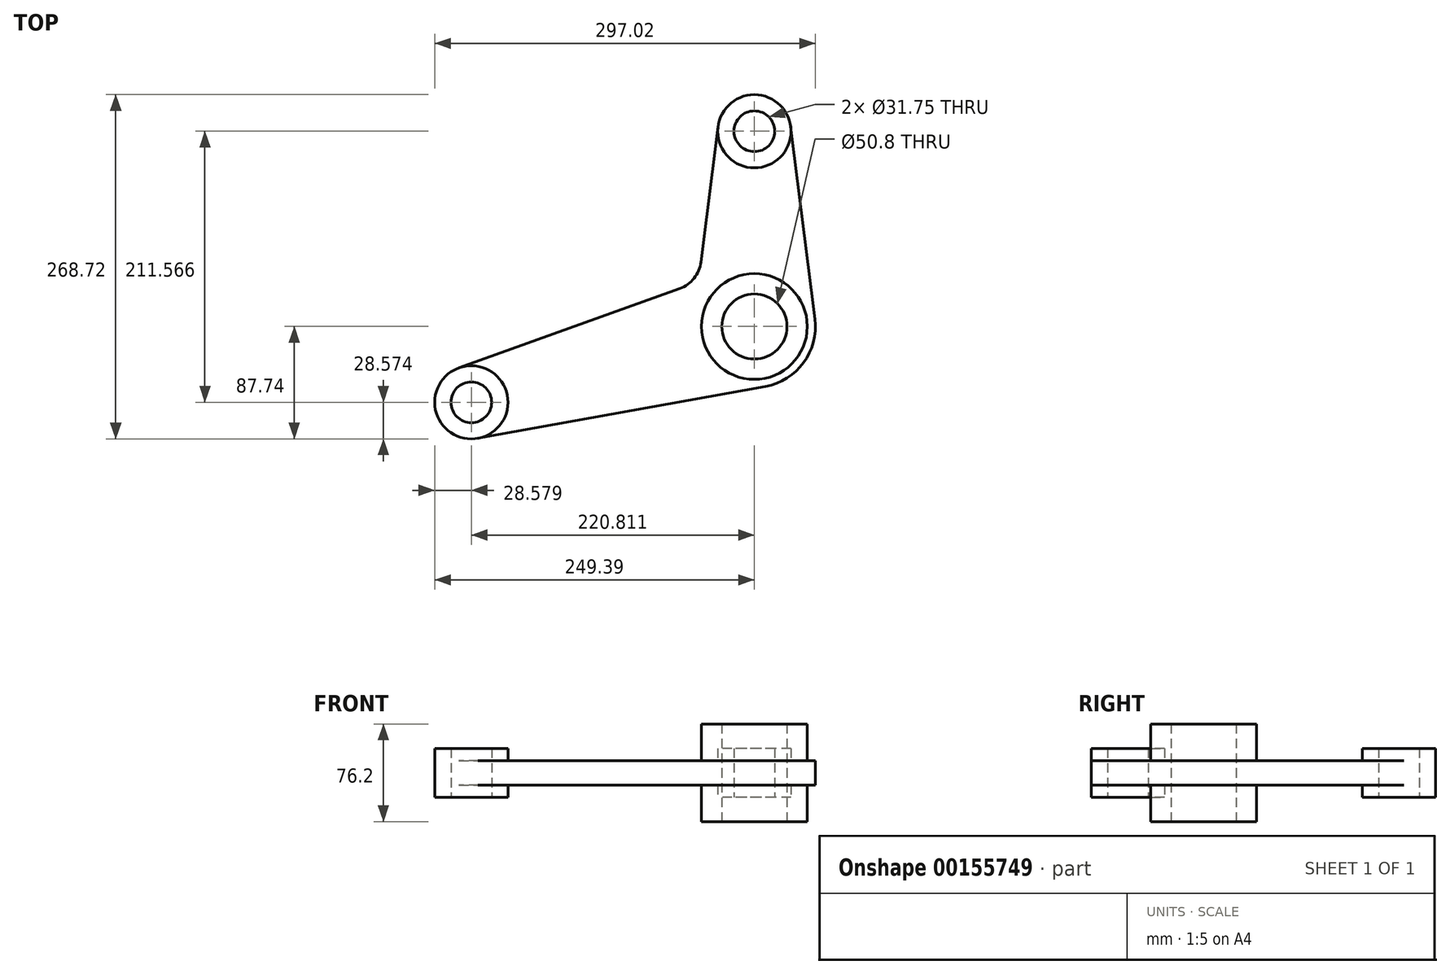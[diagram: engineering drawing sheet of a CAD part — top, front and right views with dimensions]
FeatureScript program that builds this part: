
annotation { "Feature Type Name" : "Feature", "Feature Type Description" : "" }
export const myFeature = defineFeature(function(context is Context, id is Id, definition is map)
    precondition{}
    {
        {
            var Q0;
            Q0=qCreatedBy(makeId("Top.planeOp"),FACE);
            var sketch = newSketch(context, id + "F0", { "sketchPlane" : qUnion([Q0])});
            skCircle(sketch, "E0", {"center": v(0, 0) * mm, "radius": 41.28 * mm});
            skCircle(sketch, "E1", {"center": v(0, 0) * mm, "radius": 25.4 * mm});
            skCircle(sketch, "E2", {"center": v(0, 0) * mm, "radius": 47.63 * mm});
            skCircle(sketch, "E3", {"center": v(0, 152.4) * mm, "radius": 28.58 * mm});
            skCircle(sketch, "E4", {"center": v(-220.81, -59.17) * mm, "radius": 28.58 * mm});
            skLineSegment(sketch, "E5", {"start": v(-230.48, -32.28) * mm, "end": v(-16.12, 44.82) * mm});
            skLineSegment(sketch, "E6", {"start": v(-215.74, -87.29) * mm, "end": v(8.45, -46.87) * mm});
            skLineSegment(sketch, "E7", {"start": v(-220.81, -59.17) * mm, "end": v(0, 0) * mm, "construction": true});
            skLineSegment(sketch, "E8", {"start": v(0, 152.4) * mm, "end": v(0, 0) * mm, "construction": true});
            skCircle(sketch, "E9", {"center": v(0, 152.4) * mm, "radius": 15.88 * mm});
            skCircle(sketch, "E10", {"center": v(-220.81, -59.17) * mm, "radius": 15.88 * mm});
            skLineSegment(sketch, "E11", {"start": v(-28.35, 155.97) * mm, "end": v(-47.25, 5.95) * mm});
            skLineSegment(sketch, "E12", {"start": v(28.35, 155.97) * mm, "end": v(47.25, 5.95) * mm});
            skSolve(sketch);
        }
        {
            var Q0;
            {var subQ0=sQuery(id+"F0.wireOp",EDGE,"E6");Q0=makeQuery(id+"F0.imprint","IMPRINT",FACE,{"disambiguationData":[TD([[makeQuery(id+"F0.imprint","IMPRINT",EDGE,{"derivedFrom":subQ0}),1.0]])]});}
            var Q1;
            {var subQ0=sQuery(id+"F0.wireOp",EDGE,"E5");var subQ1=sQuery(id+"F0.wireOp",EDGE,"E2");var subQ2=makeQuery(id+"F0.imprint","INTERSECT",VERTEX,{"derivedFrom":[subQ1,subQ0]});Q1=makeQuery(id+"F0.imprint","IMPRINT",FACE,{"disambiguationData":[TD([[makeQuery(id+"F0.imprint","IMPRINT",EDGE,{"disambiguationData":[TD([[subQ2,-1.0]])],"derivedFrom":subQ1}),-1.0]])]});}
            var Q2;
            Q2=makeQuery(id+"F0.imprint","IMPRINT",FACE,{"disambiguationData":[TD([[makeQuery(id+"F0.imprint","IMPRINT",EDGE,{"derivedFrom":sQuery(id+"F0.wireOp",EDGE,"E0")}),-1.0]])]});
            var Q3;
            {var subQ7=sQuery(id+"F0.wireOp",EDGE,"E12");Q3=makeQuery(id+"F0.imprint","IMPRINT",FACE,{"disambiguationData":[TD([[makeQuery(id+"F0.imprint","IMPRINT",EDGE,{"derivedFrom":subQ7}),-1.0]])]});}
            extrude(context, id + "F1", {"entities" : qUnion([Q0, Q1, Q2, Q3]), "depth" : 19.05 * mm, "symmetric" : true});
        }
        {
            var Q0;
            Q0=makeQuery(id+"F0.imprint","IMPRINT",FACE,{"disambiguationData":[TD([[makeQuery(id+"F0.imprint","IMPRINT",EDGE,{"derivedFrom":sQuery(id+"F0.wireOp",EDGE,"E0")}),1.0]])]});
            extrude(context, id + "F2", {"entities" : qUnion([Q0]), "operationType" : NewBodyOperationType.ADD, "depth" : 76.2 * mm, "symmetric" : true});
        }
        {
            var Q0;
            Q0=makeQuery(id+"F0.imprint","IMPRINT",FACE,{"disambiguationData":[TD([[makeQuery(id+"F0.imprint","IMPRINT",EDGE,{"derivedFrom":sQuery(id+"F0.wireOp",EDGE,"E10")}),-1.0]])]});
            var Q1;
            Q1=makeQuery(id+"F0.imprint","IMPRINT",FACE,{"disambiguationData":[TD([[makeQuery(id+"F0.imprint","IMPRINT",EDGE,{"derivedFrom":sQuery(id+"F0.wireOp",EDGE,"E9")}),-1.0]])]});
            extrude(context, id + "F3", {"entities" : qUnion([Q0, Q1]), "operationType" : NewBodyOperationType.ADD, "depth" : 38.1 * mm, "symmetric" : true});
        }
        {
            var Q0;
            Q0=makeQuery(id+"F1.opExtrude","SWEPT_EDGE",EDGE,{"disambiguationData":[OSD([sQuery(id+"F0.wireOp",EDGE,"E5"),sQuery(id+"F0.wireOp",EDGE,"E11")])]});
            fillet(context, id + "F4", {"entities" : qUnion([Q0]), "radius" : 25.4 * mm, "tangentPropagation" : true, "allowEdgeOverflow" : false});
        }
    });
